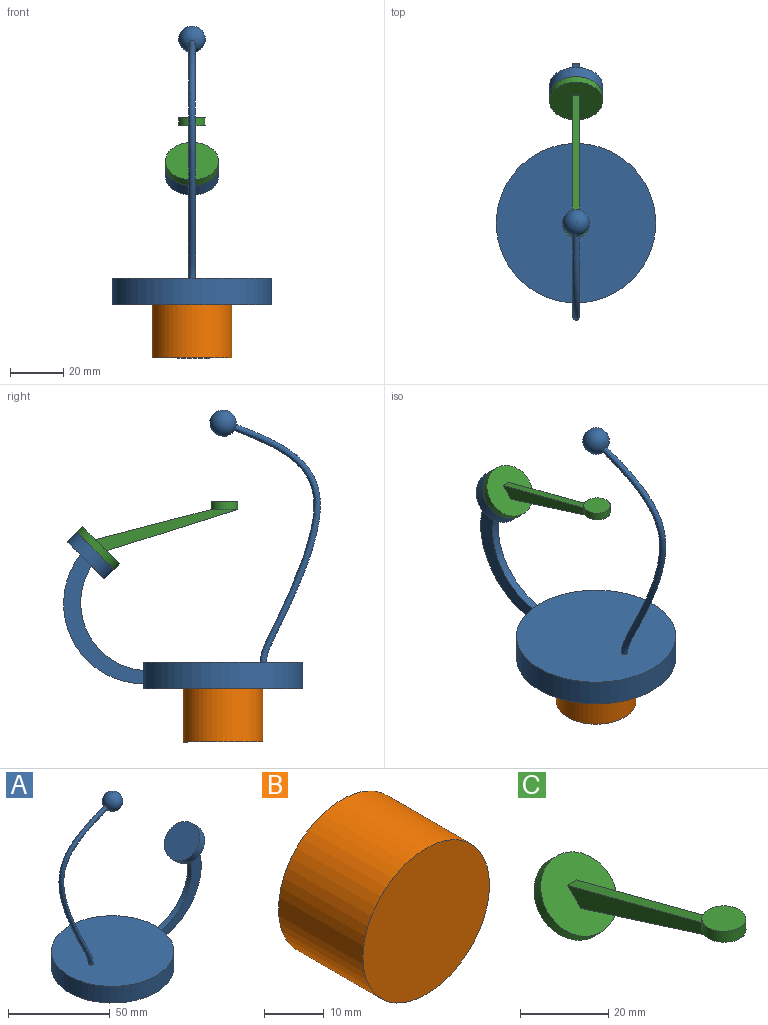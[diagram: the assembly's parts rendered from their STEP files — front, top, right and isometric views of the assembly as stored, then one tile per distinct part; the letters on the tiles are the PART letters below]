
ASSEMBLY  parts=3 mates=2
PART A: 12 faces, bbox 97.2x60.3x105.3 mm
  f0: plane 60.33x60.33mm, normal (0,0,1), area 2823mm2, adj f1,f10
  f1: cylinder r=30mm len=60mm, axis (0,0,-1), area 1869.9mm2, adj f0,f2,f3,f4,f5,f6
  f2: plane 60x60mm, normal (0,0,-1), area 2827.4mm2, adj f1
  f3: cylinder r=25.57mm len=39.41mm, axis (0,1,0), area 158.7mm2, adj f1,f5,f6,f7
  f4: cylinder r=30.18mm len=48.66mm, axis (0,1,0), area 201.5mm2, adj f1,f5,f6,f7
  f5: plane 48.66x30.05mm, normal (0,-1,0), area 365mm2, adj f1,f3,f4,f7
  f6: plane 48.66x30.05mm, normal (0,1,0), area 365mm2, adj f1,f3,f4,f7
  f7: plane 20x14.14mm, normal (0.71,0,-0.71), area 296.2mm2, adj f3,f4,f5,f6,f9
  f8: plane 20x14.14mm, normal (-0.71,0,0.71), area 314.2mm2, adj f9
  f9: cylinder r=10mm len=20mm, axis (-0.71,0,0.71), area 314.2mm2, adj f7,f8
  f10: bspline ~93.94x37.18mm, area 811.4mm2, adj f0,f11
  f11: sphere r=5mm, area 309.7mm2, adj f10
PART B: 3 faces, bbox 30x20x30 mm
  f0: cylinder r=15mm len=30mm, axis (0,1,0), area 1885mm2, adj f1,f2
  f1: plane 30x30mm, normal (0,-1,0), area 706.9mm2, adj f0
  f2: plane 30x30mm, normal (0,1,0), area 706.9mm2, adj f0
PART C: 15 faces, bbox 20x60.6x25.6 mm
  f0: plane 1.5x0.23mm, normal (0,0,1), area 0.1mm2, adj f6,f9,f13
  f1: plane 1.5x0.23mm, normal (0,0,1), area 0.1mm2, adj f6,f10,f13
  f2: plane 1.5x0.23mm, normal (0,0,1), area 0.1mm2, adj f8,f9,f13
  f3: plane 20x14.14mm, normal (0,0.71,-0.71), area 314.2mm2, adj f5
  f4: plane 20x14.14mm, normal (0,-0.71,0.71), area 296.2mm2, adj f5,f6,f8,f9,f10
  f5: cylinder r=10mm len=20mm, axis (0,-0.71,0.71), area 188.5mm2, adj f3,f4
  f6: plane 43.55x11.3mm, normal (0,0.25,0.97), area 135mm2, adj f0,f1,f4,f9,f10
  f7: plane 1.5x0.23mm, normal (0,0,1), area 0.1mm2, adj f8,f10,f13
  f8: plane 49.3x15.55mm, normal (0,-0.3,-0.95), area 155.1mm2, adj f2,f4,f7,f9,f10
  f9: plane 53.55x15.55mm, normal (1,0,0), area 194.1mm2, adj f0,f2,f4,f6,f8,f11
  f10: plane 53.55x15.55mm, normal (-1,0,0), area 194.1mm2, adj f1,f4,f6,f7,f8,f12
  f11: plane 9.54x3.5mm, normal (0,0,-1), area 24.5mm2, adj f9,f13
  f12: plane 9.54x3.5mm, normal (0,0,-1), area 24.5mm2, adj f10,f13
  f13: cylinder r=5mm len=10mm, axis (0,0,1), area 94.2mm2, adj f0,f1,f2,f7,f11,f12,f14
  f14: plane 10x10mm, normal (0,0,1), area 78.5mm2, adj f13
PLACE A rot(axis=(0,0,1),90deg) t=(-179.1,85.41,5.53)mm
PLACE B rot(axis=(-1,0,0),90deg) t=(-179.1,85.41,-14.47)mm
PLACE C t=(-179.1,117.69,53.6)mm
MATE revolute C.f5 <-> A.f9  axis (0,0.71,-0.71) through (-179.1,133.43,57.5)mm
MATE revolute A.f1 <-> B.f0  axis (0,0,-1) through (-179.1,85.41,5.53)mm
